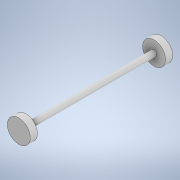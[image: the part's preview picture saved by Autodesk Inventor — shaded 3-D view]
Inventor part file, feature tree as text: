
AUTODESK INVENTOR PART (.ipt)
format: ipt  version: 2021 (Build 250183000, 183)  size: 107,520 bytes
history: native  units: mm
features: extrude x3, sketch x3
ambient origin geometry x8: Origin, YZ Plane, XZ Plane, XY Plane, X Axis, Y Axis, Z Axis, Center Point
bodies: Solid1 (feature_tree)
feature tree (6):
  extrude  "Extrusion1"  Depth=100.0mm TaperAngle=0.0deg
  extrude  "Extrusion2"  Depth=5.0mm TaperAngle=0.0deg
  extrude  "Extrusion3"  [1 undecoded]
  sketch  "Sketch1"  dims[d0=4.0mm d1=100.0mm d2=0.0mm]
  sketch  "Sketch2"  dims[d3=5.0mm d4=0.0mm d5=5.0mm d6=0.0mm]
  sketch  "Sketch3"
note: 1 required parameter value undecoded (feature->parameter linkage not recoverable at this tier; creation-order binding heuristic only, values carry confidence <= 0.55)
